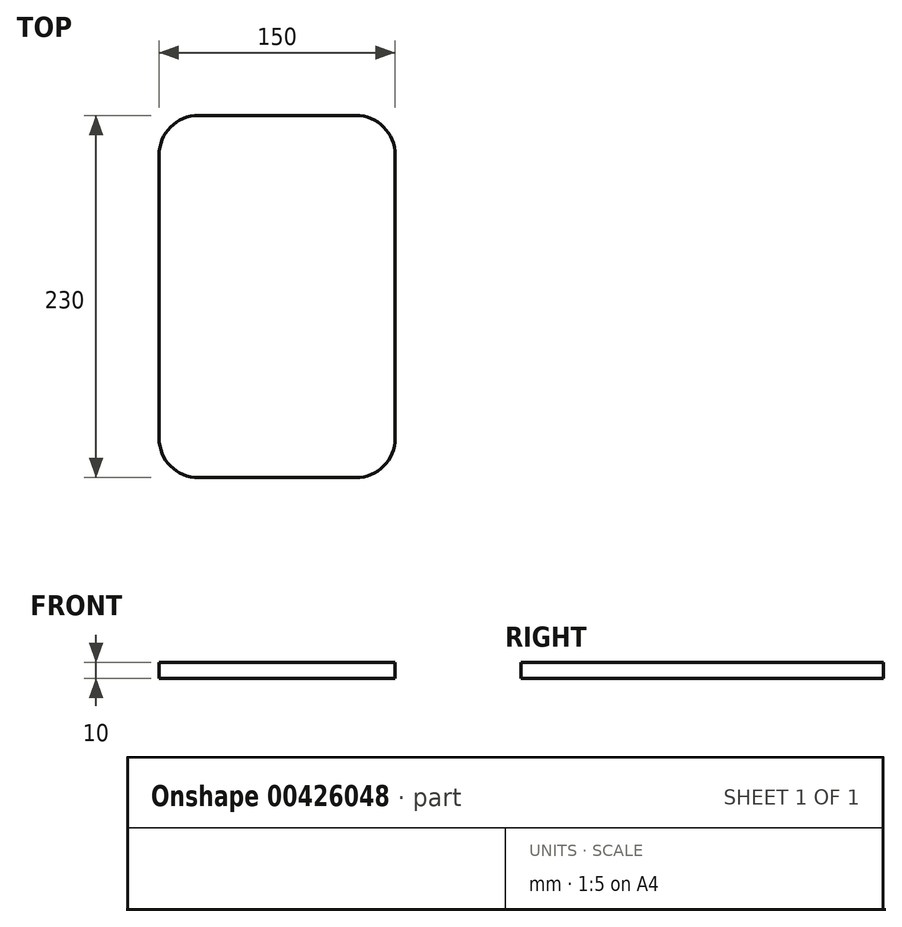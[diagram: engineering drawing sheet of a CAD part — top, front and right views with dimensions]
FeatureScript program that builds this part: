
annotation { "Feature Type Name" : "Feature", "Feature Type Description" : "" }
export const myFeature = defineFeature(function(context is Context, id is Id, definition is map)
    precondition{}
    {
        {
            var Q0;
            Q0=qCreatedBy(makeId("Top.planeOp"),FACE);
            var sketch = newSketch(context, id + "F0", { "sketchPlane" : qUnion([Q0])});
            skLineSegment(sketch, "E0.bottom", {"start": v(53.28, -155) * mm, "end": v(-46.72, -155) * mm});
            skLineSegment(sketch, "E0.top", {"start": v(53.28, 75) * mm, "end": v(-46.72, 75) * mm});
            skLineSegment(sketch, "E0.left", {"start": v(78.28, -130) * mm, "end": v(78.28, 50) * mm});
            skLineSegment(sketch, "E0.right", {"start": v(-71.72, -130) * mm, "end": v(-71.72, 50) * mm});
            skLineSegment(sketch, "E1", {"start": v(-71.72, -40) * mm, "end": v(78.28, -40) * mm, "construction": true});
            skLineSegment(sketch, "E2", {"start": v(3.28, 75) * mm, "end": v(3.28, -155) * mm, "construction": true});
            skLineSegment(sketch, "E3", {"start": v(-71.72, 75) * mm, "end": v(78.28, -155) * mm, "construction": true});
            skLineSegment(sketch, "E4", {"start": v(-71.72, -155) * mm, "end": v(78.28, 75) * mm, "construction": true});
            skCircle(sketch, "E5", {"center": v(-84.22, 94.17) * mm, "radius": 1.5 * mm});
            skCircle(sketch, "E6.MirrorC", {"center": v(90.78, 94.17) * mm, "radius": 1.5 * mm});
            skCircle(sketch, "E7.MirrorC", {"center": v(90.78, -174.17) * mm, "radius": 1.5 * mm});
            skCircle(sketch, "E8.MirrorC", {"center": v(-84.22, -174.17) * mm, "radius": 1.5 * mm});
            skPoint(sketch, "E9.visualSharp", {"position": v(-71.72, 75) * mm});
            skArc(sketch, "E9.filletArc", {"start": v(-46.72, 75) * mm, "mid": v(-64.4, 67.68) * mm, "end": v(-71.72, 50) * mm});
            skPoint(sketch, "E10.visualSharp", {"position": v(-71.72, -155) * mm});
            skArc(sketch, "E10.filletArc", {"start": v(-71.72, -130) * mm, "mid": v(-64.4, -147.68) * mm, "end": v(-46.72, -155) * mm});
            skPoint(sketch, "E11.visualSharp", {"position": v(78.28, -155) * mm});
            skArc(sketch, "E11.filletArc", {"start": v(53.28, -155) * mm, "mid": v(70.96, -147.68) * mm, "end": v(78.28, -130) * mm});
            skPoint(sketch, "E12.visualSharp", {"position": v(78.28, 75) * mm});
            skArc(sketch, "E12.filletArc", {"start": v(78.28, 50) * mm, "mid": v(70.96, 67.68) * mm, "end": v(53.28, 75) * mm});
            skLineSegment(sketch, "E13", {"start": v(-46.72, -155) * mm, "end": v(-46.72, 75) * mm, "construction": true});
            skLineSegment(sketch, "E14.MirrorCS", {"start": v(53.28, -155) * mm, "end": v(53.28, 75) * mm, "construction": true});
            skSolve(sketch);
        }
        {
            var Q0;
            Q0=makeQuery(id+"F0.imprint","IMPRINT",FACE,{"disambiguationData":[TD([[makeQuery(id+"F0.imprint","IMPRINT",EDGE,{"derivedFrom":sQuery(id+"F0.wireOp",EDGE,"E0.bottom")}),-1.0]])]});
            extrude(context, id + "F1", {"entities" : qUnion([Q0]), "depth" : 10 * mm});
        }
    });
